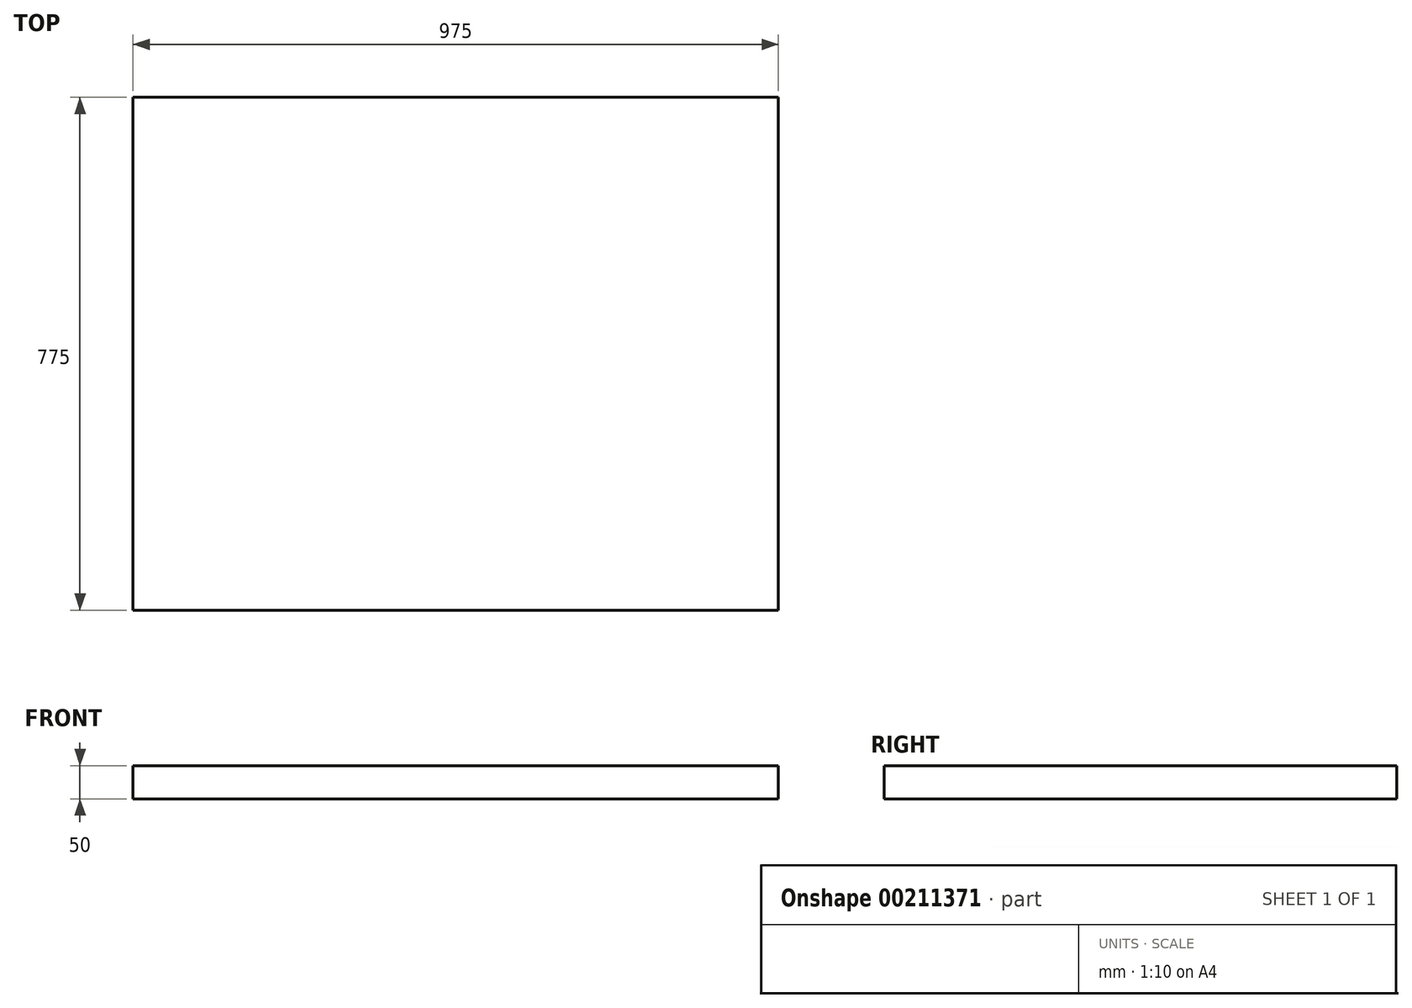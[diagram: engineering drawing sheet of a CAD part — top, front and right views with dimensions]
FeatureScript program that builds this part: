
annotation { "Feature Type Name" : "Feature", "Feature Type Description" : "" }
export const myFeature = defineFeature(function(context is Context, id is Id, definition is map)
    precondition{}
    {
        {
            var Q0;
            Q0=qCreatedBy(makeId("Top.planeOp"),FACE);
            var sketch = newSketch(context, id + "F0", { "sketchPlane" : qUnion([Q0])});
            skLineSegment(sketch, "E0.bottom", {"start": v(-487.12, 314.1) * mm, "end": v(487.88, 314.1) * mm});
            skLineSegment(sketch, "E0.top", {"start": v(-487.12, -460.9) * mm, "end": v(487.88, -460.9) * mm});
            skLineSegment(sketch, "E0.left", {"start": v(-487.12, 314.1) * mm, "end": v(-487.12, -460.9) * mm});
            skLineSegment(sketch, "E0.right", {"start": v(487.88, 314.1) * mm, "end": v(487.88, -460.9) * mm});
            skSolve(sketch);
        }
        {
            var Q0;
            Q0=makeQuery(id+"F0.imprint","IMPRINT",FACE,{"disambiguationData":[TD([[makeQuery(id+"F0.imprint","IMPRINT",EDGE,{"derivedFrom":sQuery(id+"F0.wireOp",EDGE,"E0.bottom")}),-1.0]])]});
            extrude(context, id + "F1", {"entities" : qUnion([Q0]), "depth" : 50 * mm});
        }
    });
